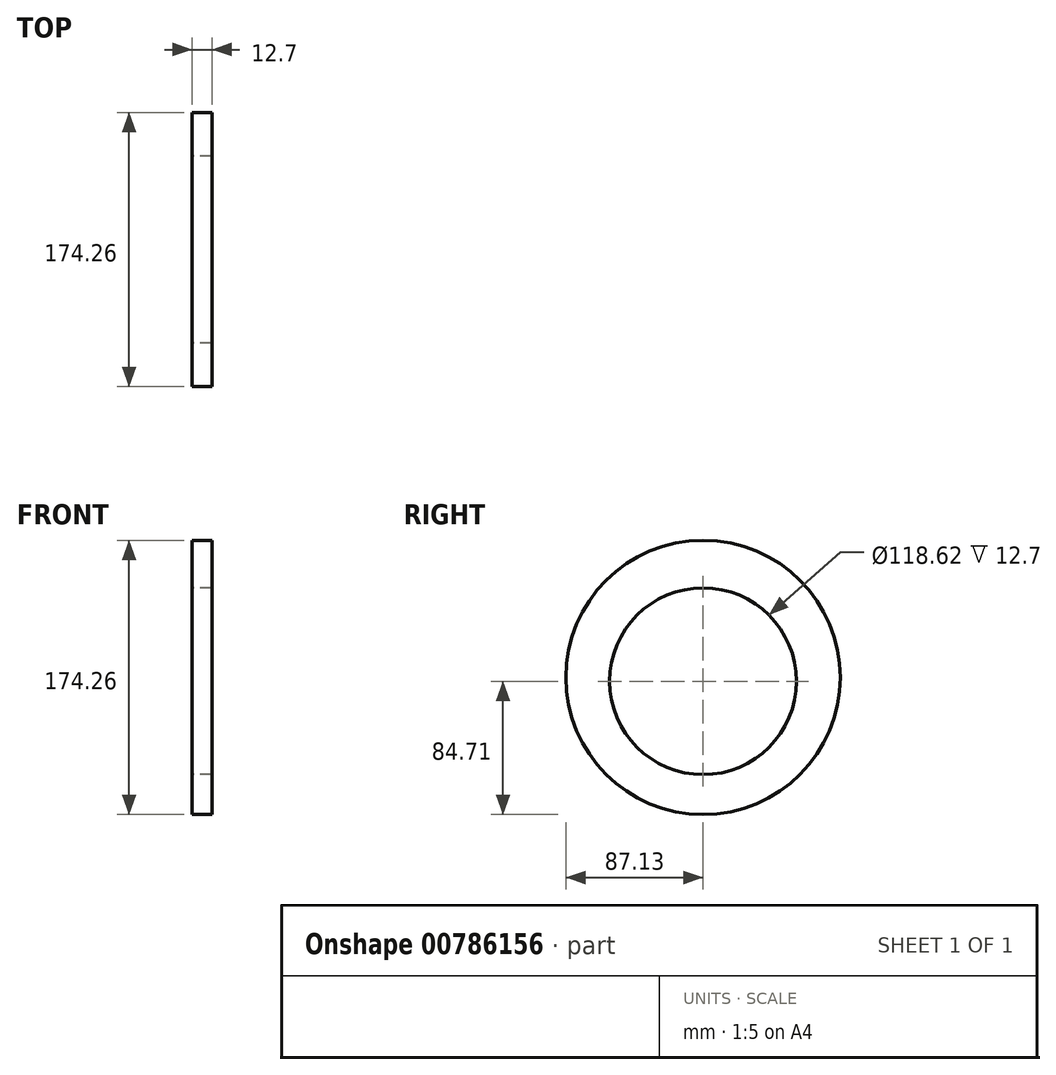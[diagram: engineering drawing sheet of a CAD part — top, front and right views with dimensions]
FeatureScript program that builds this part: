
annotation { "Feature Type Name" : "Feature", "Feature Type Description" : "" }
export const myFeature = defineFeature(function(context is Context, id is Id, definition is map)
    precondition{}
    {
        {
            var Q0;
            Q0=qCreatedBy(makeId("Right.planeOp"),FACE);
            var sketch = newSketch(context, id + "F0", { "sketchPlane" : qUnion([Q0])});
            skCircle(sketch, "E0", {"center": v(0, 2.42) * mm, "radius": 87.13 * mm});
            skCircle(sketch, "E1", {"center": v(0, 0) * mm, "radius": 59.3 * mm});
            skSolve(sketch);
        }
        {
            var Q0;
            Q0 = qSketchRegion(id + "F0", true);
            extrude(context, id + "F1", {"entities" : qUnion([Q0]), "depth" : 12.7 * mm, "offsetDistance" : 25.4 * mm});
        }
    });
